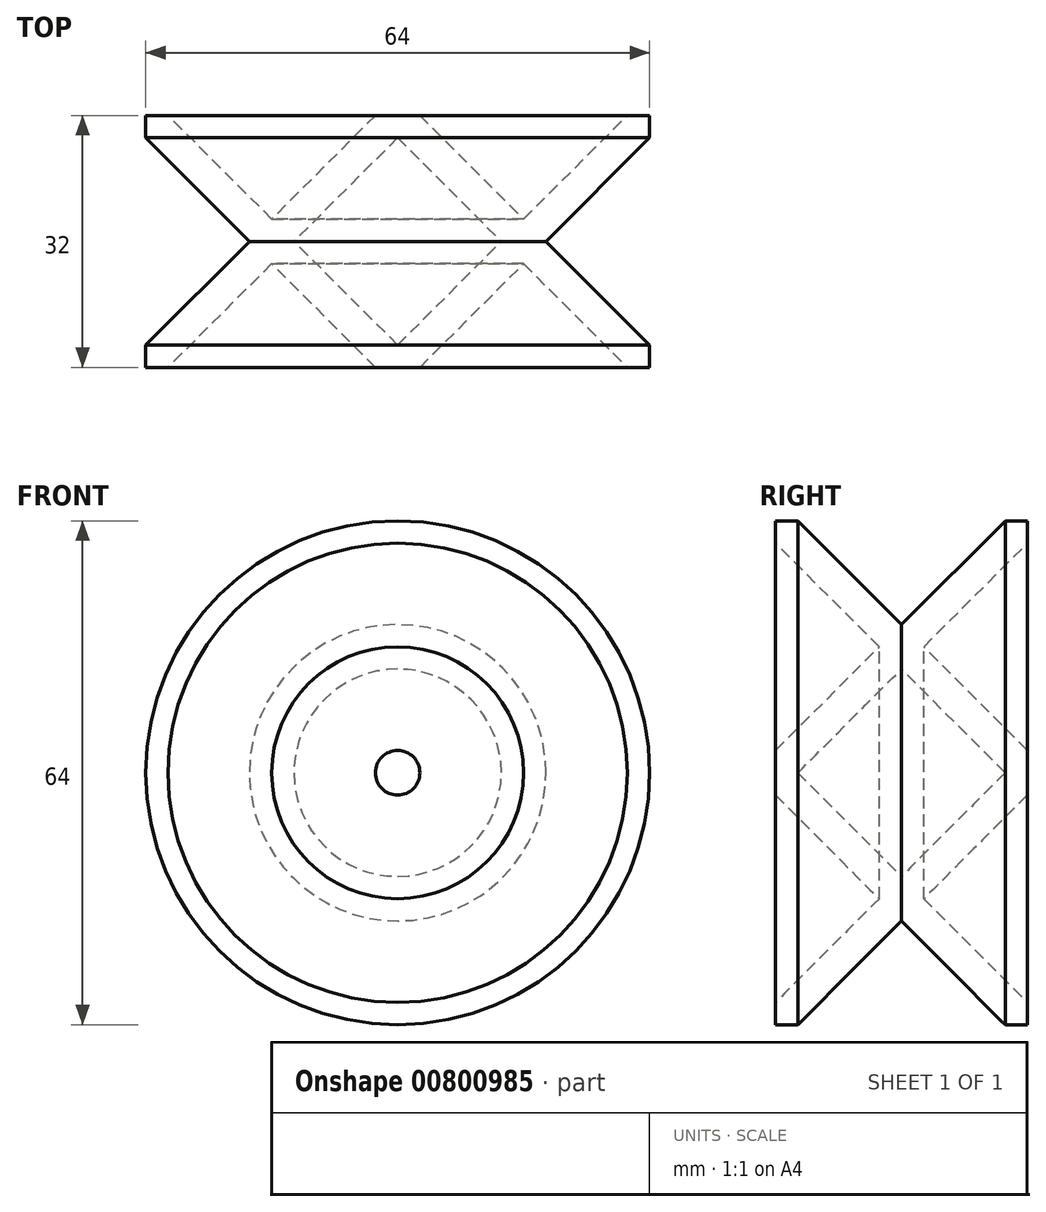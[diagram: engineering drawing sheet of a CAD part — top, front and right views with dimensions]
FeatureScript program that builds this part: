
annotation { "Feature Type Name" : "Feature", "Feature Type Description" : "" }
export const myFeature = defineFeature(function(context is Context, id is Id, definition is map)
    precondition{}
    {
        {
            var Q0;
            Q0=qCreatedBy(makeId("Top.planeOp"),FACE);
            var sketch = newSketch(context, id + "F0", { "sketchPlane" : qUnion([Q0])});
            skLineSegment(sketch, "E0", {"start": v(0, 0) * mm, "end": v(2.83, 0) * mm});
            skLineSegment(sketch, "E1", {"start": v(2.83, 0) * mm, "end": v(16, -13.17) * mm});
            skLineSegment(sketch, "E2", {"start": v(16, -13.17) * mm, "end": v(29.17, 0) * mm});
            skLineSegment(sketch, "E3", {"start": v(29.17, 0) * mm, "end": v(32, 0) * mm});
            skLineSegment(sketch, "E4", {"start": v(32, 0) * mm, "end": v(32, -2.83) * mm});
            skLineSegment(sketch, "E5", {"start": v(32, -2.83) * mm, "end": v(18.83, -16) * mm});
            skLineSegment(sketch, "E6", {"start": v(18.83, -16) * mm, "end": v(32, -29.17) * mm});
            skLineSegment(sketch, "E7", {"start": v(32, -29.17) * mm, "end": v(32, -32) * mm});
            skLineSegment(sketch, "E8", {"start": v(32, -32) * mm, "end": v(29.17, -32) * mm});
            skLineSegment(sketch, "E9", {"start": v(29.17, -32) * mm, "end": v(16, -18.83) * mm});
            skLineSegment(sketch, "E10", {"start": v(16, -18.83) * mm, "end": v(2.83, -32) * mm});
            skLineSegment(sketch, "E11", {"start": v(2.83, -32) * mm, "end": v(0, -32) * mm});
            skLineSegment(sketch, "E12", {"start": v(0, -32) * mm, "end": v(0, -29.17) * mm});
            skLineSegment(sketch, "E13", {"start": v(0, -29.17) * mm, "end": v(13.17, -16) * mm});
            skLineSegment(sketch, "E14", {"start": v(13.17, -16) * mm, "end": v(0, -2.83) * mm});
            skLineSegment(sketch, "E15", {"start": v(0, -2.83) * mm, "end": v(0, 0) * mm});
            skSolve(sketch);
        }
        {
            var Q0;
            Q0=makeQuery(id+"F0.imprint","IMPRINT",FACE,{"disambiguationData":[TD([[makeQuery(id+"F0.imprint","IMPRINT",EDGE,{"derivedFrom":sQuery(id+"F0.wireOp",EDGE,"E0")}),-1.0]])]});
            var Q1;
            Q1=sQuery(id+"F0.wireOp",EDGE,"E15");
            revolve(context, id + "F1", {"surfaceOperationType" : NewSurfaceOperationType.NEW, "entities" : qUnion([Q0]), "axis" : qUnion([Q1]), "revolveType" : RevolveType.FULL});
        }
    });
